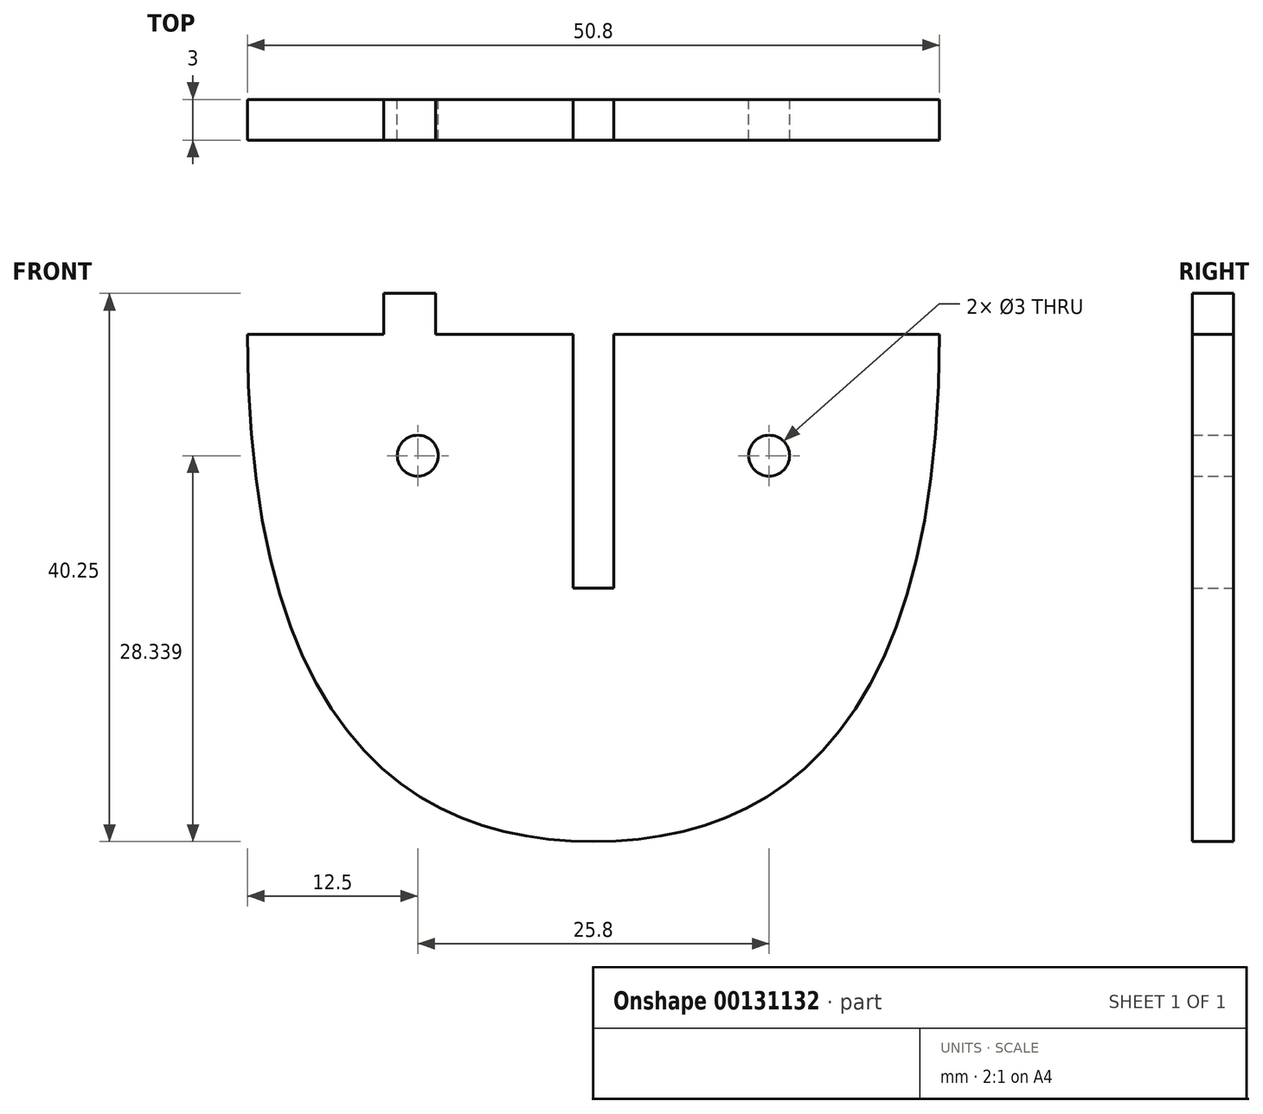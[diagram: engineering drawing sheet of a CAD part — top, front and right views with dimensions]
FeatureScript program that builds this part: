
annotation { "Feature Type Name" : "Feature", "Feature Type Description" : "" }
export const myFeature = defineFeature(function(context is Context, id is Id, definition is map)
    precondition{}
    {
        {
            var Q0;
            Q0=qCreatedBy(makeId("Front.planeOp"),FACE);
            var sketch = newSketch(context, id + "F0", { "sketchPlane" : qUnion([Q0])});
            skLineSegment(sketch, "E0", {"start": v(0, 0) * mm, "end": v(25.4, 0) * mm});
            skLineSegment(sketch, "E1", {"start": v(0, 0) * mm, "end": v(-25.4, 0) * mm});
            skLineSegment(sketch, "E2", {"start": v(0, 0) * mm, "end": v(0, -37.25) * mm});
            skFitSpline(sketch, "E3", {"points": [v(-25.4, 0) * mm, v(0, -37.25) * mm, v(25.4, 0) * mm], "startDerivative": vector(0, -180) * mm, "endDerivative": vector(0, 180) * mm});
            skLineSegment(sketch, "E4", {"start": v(25.4, 0) * mm, "end": v(25.4, -30) * mm});
            skLineSegment(sketch, "E5", {"start": v(-25.4, 0) * mm, "end": v(-25.4, -30) * mm});
            skLineSegment(sketch, "E6", {"start": v(-25.4, 0) * mm, "end": v(-15.4, 0) * mm});
            skLineSegment(sketch, "E7", {"start": v(25.4, 0) * mm, "end": v(15.4, 0) * mm});
            skLineSegment(sketch, "E8.bottom", {"start": v(-15.4, 0) * mm, "end": v(-11.6, 0) * mm});
            skLineSegment(sketch, "E8.top", {"start": v(-15.4, 3) * mm, "end": v(-11.6, 3) * mm});
            skLineSegment(sketch, "E8.left", {"start": v(-15.4, 0) * mm, "end": v(-15.4, 3) * mm});
            skLineSegment(sketch, "E8.right", {"start": v(-11.6, 0) * mm, "end": v(-11.6, 3) * mm});
            skLineSegment(sketch, "E9.bottom", {"start": v(15.4, 0) * mm, "end": v(11.6, 0) * mm});
            skLineSegment(sketch, "E9.top", {"start": v(15.4, 3) * mm, "end": v(11.6, 3) * mm});
            skLineSegment(sketch, "E9.left", {"start": v(15.4, 0) * mm, "end": v(15.4, 3) * mm});
            skLineSegment(sketch, "E9.right", {"start": v(11.6, 0) * mm, "end": v(11.6, 3) * mm});
            skLineSegment(sketch, "E10", {"start": v(0, 0) * mm, "end": v(0, -9.32) * mm});
            skLineSegment(sketch, "E11.bottom", {"start": v(-1.5, 0) * mm, "end": v(1.5, 0) * mm});
            skLineSegment(sketch, "E11.top", {"start": v(-1.5, -18.63) * mm, "end": v(1.5, -18.63) * mm});
            skLineSegment(sketch, "E11.left", {"start": v(-1.5, 0) * mm, "end": v(-1.5, -18.63) * mm});
            skLineSegment(sketch, "E11.right", {"start": v(1.5, 0) * mm, "end": v(1.5, -18.63) * mm});
            skPoint(sketch, "E11.middle", {"position": v(0, -9.32) * mm});
            skLineSegment(sketch, "E12.bottom", {"start": v(-11.6, 0) * mm, "end": v(-7.6, 0) * mm});
            skLineSegment(sketch, "E13", {"start": v(-25.4, 0) * mm, "end": v(6.35, 0) * mm});
            skLineSegment(sketch, "E14.bottom", {"start": v(-17.05, 0) * mm, "end": v(4.35, 0) * mm});
            skCircle(sketch, "E15", {"center": v(-12.9, -8.91) * mm, "radius": 1.5 * mm});
            skCircle(sketch, "E16", {"center": v(12.9, -8.91) * mm, "radius": 1.5 * mm});
            skSolve(sketch);
        }
        {
            var Q0;
            Q0=makeQuery(id+"F0.imprint","IMPRINT",FACE,{"disambiguationData":[TD([[makeQuery(id+"F0.imprint","IMPRINT",EDGE,{"derivedFrom":sQuery(id+"F0.wireOp",EDGE,"E1")}),1.0]])]});
            var Q1;
            Q1=makeQuery(id+"F0.imprint","IMPRINT",FACE,{"disambiguationData":[TD([[makeQuery(id+"F0.imprint","IMPRINT",EDGE,{"derivedFrom":sQuery(id+"F0.wireOp",EDGE,"E0")}),-1.0]])]});
            var Q2;
            Q2=makeQuery(id+"F0.imprint","IMPRINT",FACE,{"disambiguationData":[TD([[makeQuery(id+"F0.imprint","IMPRINT",EDGE,{"derivedFrom":sQuery(id+"F0.wireOp",EDGE,"E9.bottom")}),-1.0]])]});
            var Q3;
            Q3=makeQuery(id+"F0.imprint","IMPRINT",FACE,{"disambiguationData":[TD([[makeQuery(id+"F0.imprint","IMPRINT",EDGE,{"derivedFrom":sQuery(id+"F0.wireOp",EDGE,"E8.top")}),-1.0]])]});
            var Q4;
            Q4=makeQuery(id+"F0.imprint","IMPRINT",FACE,{"disambiguationData":[TD([[makeQuery(id+"F0.imprint","IMPRINT",EDGE,{"derivedFrom":sQuery(id+"F0.wireOp",EDGE,"QJXkaJoY-NPPO-3JZ7-Pn2X-T86UCE4SSyNz.bottom")}),1.0]])]});
            var Q5;
            {var subQ0=sQuery(id+"F0.wireOp",EDGE,"E11.left");Q5=makeQuery(id+"F0.imprint","IMPRINT",FACE,{"disambiguationData":[TD([[makeQuery(id+"F0.imprint","IMPRINT",EDGE,{"derivedFrom":subQ0}),-1.0]])]});}
            extrude(context, id + "F1", {"entities" : qUnion([Q0, Q1, Q2, Q3, Q4, Q5]), "depth" : 3 * mm});
        }
    });
